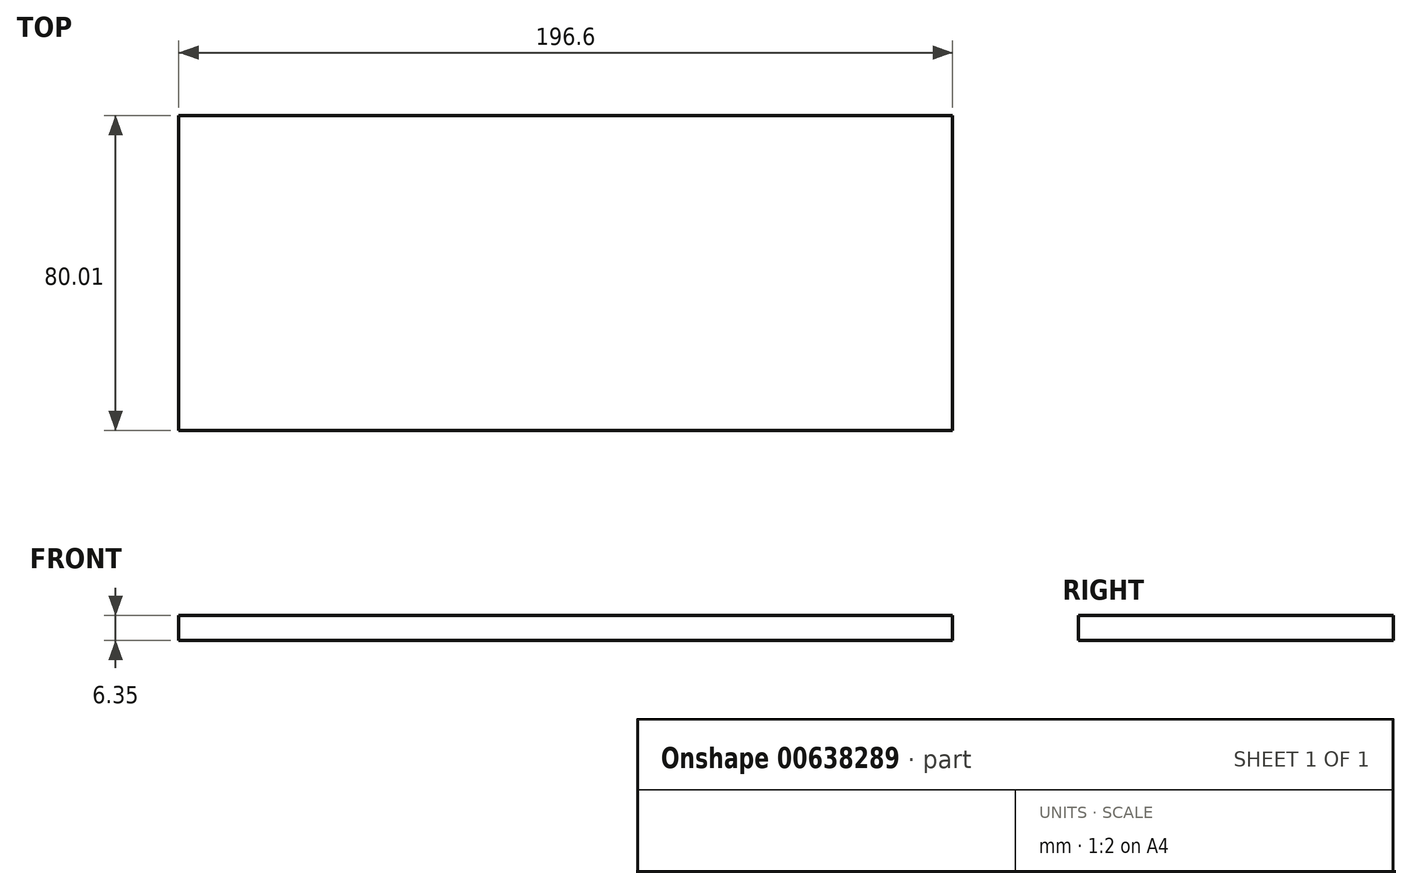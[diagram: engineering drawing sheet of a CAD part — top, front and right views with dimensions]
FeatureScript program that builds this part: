
annotation { "Feature Type Name" : "Feature", "Feature Type Description" : "" }
export const myFeature = defineFeature(function(context is Context, id is Id, definition is map)
    precondition{}
    {
        {
            var Q0;
            Q0=qCreatedBy(makeId("Top.planeOp"),FACE);
            var sketch = newSketch(context, id + "F0", { "sketchPlane" : qUnion([Q0])});
            skLineSegment(sketch, "E0.bottom", {"start": v(0, 0) * mm, "end": v(196.6, 0) * mm});
            skLineSegment(sketch, "E0.top", {"start": v(0, -80) * mm, "end": v(196.6, -80) * mm});
            skLineSegment(sketch, "E0.left", {"start": v(0, 0) * mm, "end": v(0, -80) * mm});
            skLineSegment(sketch, "E0.right", {"start": v(196.6, 0) * mm, "end": v(196.6, -80) * mm});
            skSolve(sketch);
        }
        {
            var Q0;
            Q0=makeQuery(id+"F0.imprint","IMPRINT",FACE,{"disambiguationData":[TD([[makeQuery(id+"F0.imprint","IMPRINT",EDGE,{"derivedFrom":sQuery(id+"F0.wireOp",EDGE,"E0.bottom")}),-1.0]])]});
            extrude(context, id + "F1", {"entities" : qUnion([Q0]), "depth" : 6.35 * mm, "offsetDistance" : 25.4 * mm});
        }
    });
